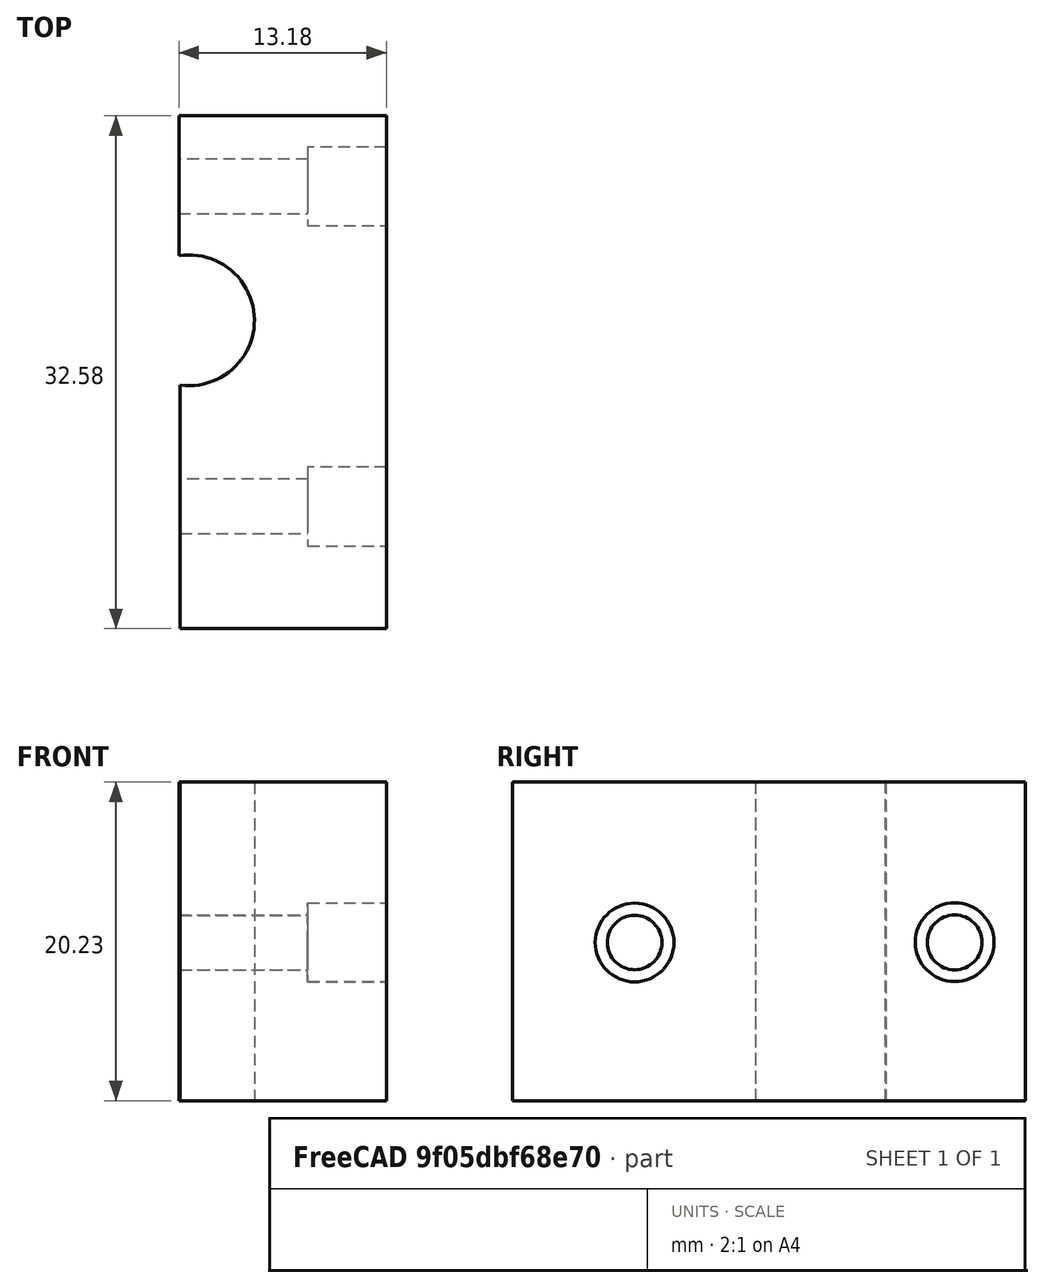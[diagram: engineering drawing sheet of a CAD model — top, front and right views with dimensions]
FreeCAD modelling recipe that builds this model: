
FCSTD DOCUMENT  (FreeCAD 2024.2R37179 (Git))
Label: front_rod_holder
License: All rights reserved
LicenseURL: http://en.wikipedia.org/wiki/All_rights_reserved
objects: PartDesign::Pocket×2, Part::Feature×1, PartDesign::FeatureBase×1, Sketcher::SketchObject×1, PartDesign::Body×1
note: 8 computed .brp shape members not serialized (recipe doc carries the construction recipe); baked Part::Feature solids carry a one-line shape summary decoded from their .brp

FEATURE [Part::Feature] Pocket001
  Placement = pos=(0,0,0) rot=(1,0,0;1.5708rad)
  shape: bbox 16.18 x 20.23 x 32.58 mm, 10 faces (baked)
FEATURE [PartDesign::FeatureBase] BaseFeature
  BaseFeature = -> Pocket001
  Suppressed = false
FEATURE [PartDesign::Pocket] Pocket
  BaseFeature = -> BaseFeature
  Direction = (-1,0,0)
  Length = 3
  Length2 = 5
  Profile = -> BaseFeature [Face10]
  Refine = true
  Suppressed = false
  Type = 0
FEATURE [Sketcher::SketchObject] Sketch
  AttachmentSupport = -> [Pocket]
  FullyConstrained = false
  MapMode = 5
  Placement = pos=(32.7545,0,0) rot=(0.57735,0.57735,0.57735;2.0944rad)
  sketch-geometry (2):
    g0: Circle CenterX=65.7728 CenterY=-131.954 CenterZ=0 NormalX=0 NormalY=0 NormalZ=1 AngleXU=0 Radius=2.5
    g1: Circle CenterX=86.1054 CenterY=-131.936 CenterZ=0 NormalX=0 NormalY=0 NormalZ=1 AngleXU=0 Radius=2.5
  constraints (2):
    c: Diameter(g0) = 5
    c: Diameter(g1) = 5
FEATURE [PartDesign::Pocket] Pocket002
  BaseFeature = -> Pocket
  Direction = (-1,0,0)
  Length = 5
  Length2 = 5
  Profile = -> Sketch
  ReferenceAxis = -> Sketch [N_Axis]
  Refine = true
  Suppressed = false
  Type = 0
FEATURE [PartDesign::Body] Body
  BaseFeature = -> Pocket001
  Group = -> [BaseFeature,Pocket,Sketch,Pocket002]
  Origin = -> Origin
  Tip = -> Pocket002
